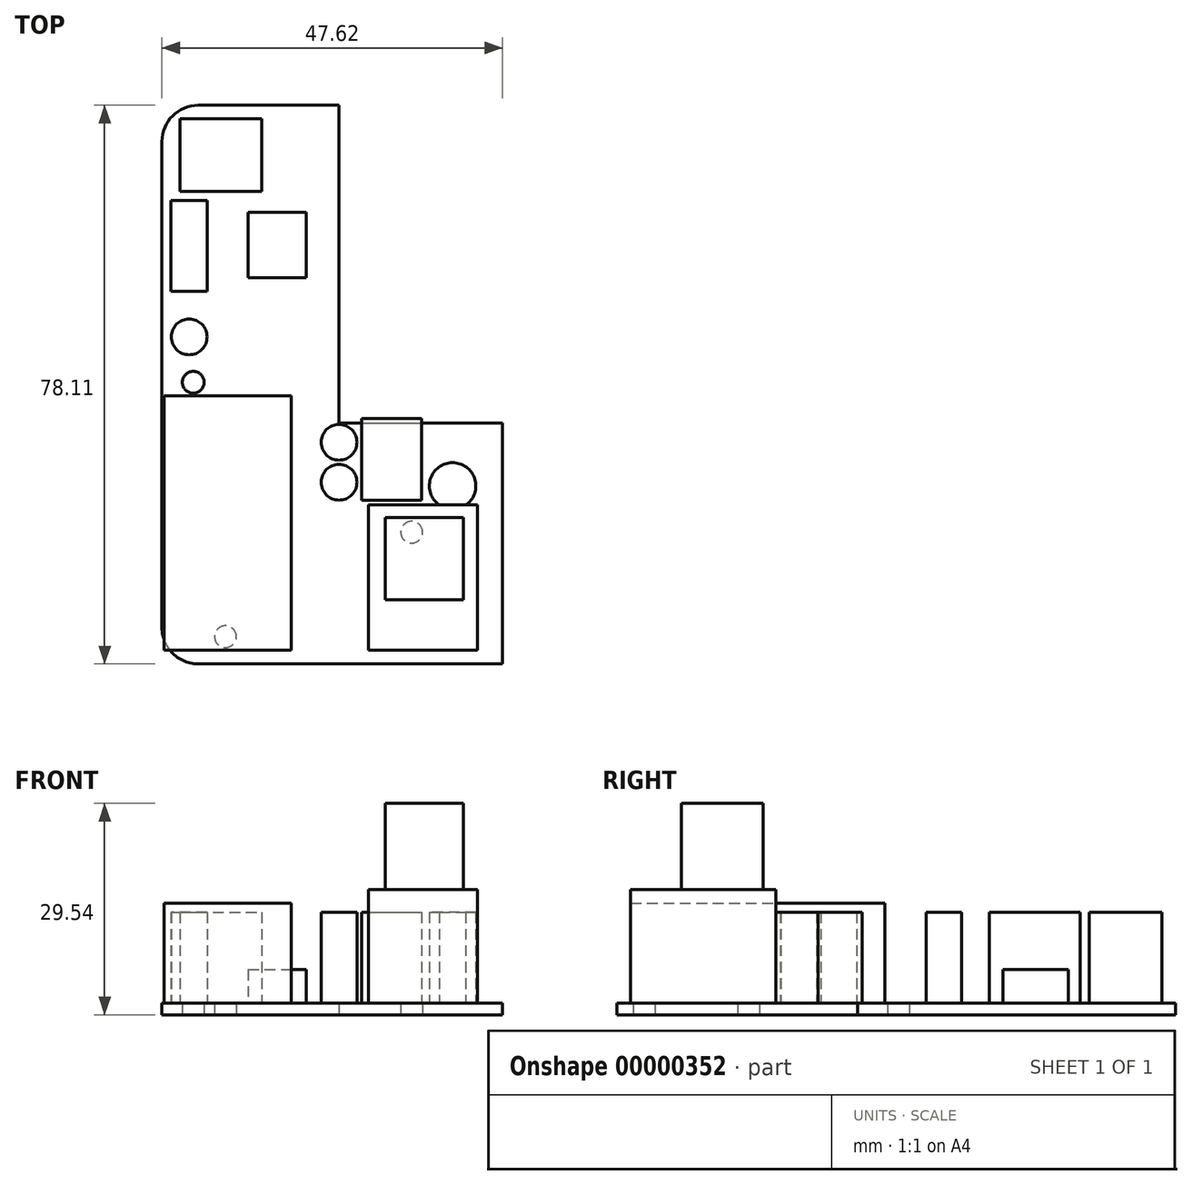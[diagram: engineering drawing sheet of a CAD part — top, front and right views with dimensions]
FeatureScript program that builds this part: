
annotation { "Feature Type Name" : "Feature", "Feature Type Description" : "" }
export const myFeature = defineFeature(function(context is Context, id is Id, definition is map)
    precondition{}
    {
        {
            var Q0;
            Q0=qCreatedBy(makeId("Top.planeOp"),FACE);
            var sketch = newSketch(context, id + "F0", { "sketchPlane" : qUnion([Q0])});
            skLineSegment(sketch, "E0.bottom", {"start": v(5.08, 78.1) * mm, "end": v(24.76, 78.1) * mm});
            skLineSegment(sketch, "E0.top", {"start": v(5.08, 0) * mm, "end": v(24.77, 0) * mm});
            skLineSegment(sketch, "E0.left", {"start": v(0, 73.03) * mm, "end": v(0, 5.08) * mm});
            skLineSegment(sketch, "E0.right", {"start": v(24.76, 78.1) * mm, "end": v(24.77, 33.65) * mm});
            skLineSegment(sketch, "E1.bottom", {"start": v(24.77, 0) * mm, "end": v(47.62, 0) * mm});
            skLineSegment(sketch, "E1.top", {"start": v(24.77, 33.65) * mm, "end": v(47.62, 33.65) * mm});
            skLineSegment(sketch, "E1.right", {"start": v(47.63, 0) * mm, "end": v(47.62, 33.65) * mm});
            skPoint(sketch, "E2.visualSharp", {"position": v(0, 78.1) * mm});
            skArc(sketch, "E2.filletArc", {"start": v(5.08, 78.1) * mm, "mid": v(1.49, 76.62) * mm, "end": v(0, 73.03) * mm});
            skPoint(sketch, "E3.visualSharp", {"position": v(0, 0) * mm});
            skArc(sketch, "E3.filletArc", {"start": v(0, 5.08) * mm, "mid": v(1.49, 1.49) * mm, "end": v(5.08, 0) * mm});
            skCircle(sketch, "E4", {"center": v(4.38, 39.38) * mm, "radius": 1.52 * mm});
            skCircle(sketch, "E5", {"center": v(8.9, 3.81) * mm, "radius": 1.52 * mm});
            skCircle(sketch, "E6", {"center": v(34.92, 18.41) * mm, "radius": 1.52 * mm});
            skSolve(sketch);
        }
        {
            var Q0;
            Q0=qSketchRegion(id+"F0",true);
            extrude(context, id + "F1", {"entities" : qUnion([Q0]), "depth" : 1.6 * mm});
        }
        {
            var Q0;
            Q0=makeQuery(id+"F1.opExtrude","CAP_FACE",FACE,{"disambiguationData":[OSD([sQuery(id+"F0.wireOp",EDGE,"E0.bottom"),sQuery(id+"F0.wireOp",EDGE,"E0.top"),sQuery(id+"F0.wireOp",EDGE,"E0.left"),sQuery(id+"F0.wireOp",EDGE,"E0.right"),sQuery(id+"F0.wireOp",EDGE,"E1.bottom"),sQuery(id+"F0.wireOp",EDGE,"E1.top"),sQuery(id+"F0.wireOp",EDGE,"E1.right"),sQuery(id+"F0.wireOp",EDGE,"E2.filletArc"),sQuery(id+"F0.wireOp",EDGE,"E3.filletArc"),sQuery(id+"F0.wireOp",EDGE,"E4"),sQuery(id+"F0.wireOp",EDGE,"E5"),sQuery(id+"F0.wireOp",EDGE,"E6")])],"isStart":false});
            var sketch = newSketch(context, id + "F2", { "sketchPlane" : qUnion([Q0])});
            skLineSegment(sketch, "E7.bottom", {"start": v(2.54, 76.2) * mm, "end": v(13.97, 76.2) * mm});
            skLineSegment(sketch, "E7.top", {"start": v(2.54, 66.04) * mm, "end": v(13.97, 66.04) * mm});
            skLineSegment(sketch, "E7.left", {"start": v(2.54, 76.2) * mm, "end": v(2.54, 66.04) * mm});
            skLineSegment(sketch, "E7.right", {"start": v(13.97, 76.2) * mm, "end": v(13.97, 66.04) * mm});
            skLineSegment(sketch, "E8.bottom", {"start": v(1.27, 64.77) * mm, "end": v(6.35, 64.77) * mm});
            skLineSegment(sketch, "E8.top", {"start": v(1.27, 52.07) * mm, "end": v(6.35, 52.07) * mm});
            skLineSegment(sketch, "E8.left", {"start": v(1.27, 64.77) * mm, "end": v(1.27, 52.07) * mm});
            skLineSegment(sketch, "E8.right", {"start": v(6.35, 64.77) * mm, "end": v(6.35, 52.07) * mm});
            skLineSegment(sketch, "E9.bottom", {"start": v(27.94, 34.3) * mm, "end": v(36.32, 34.3) * mm});
            skLineSegment(sketch, "E9.top", {"start": v(27.94, 22.86) * mm, "end": v(36.32, 22.86) * mm});
            skLineSegment(sketch, "E9.left", {"start": v(27.94, 34.3) * mm, "end": v(27.94, 22.86) * mm});
            skLineSegment(sketch, "E9.right", {"start": v(36.32, 34.3) * mm, "end": v(36.32, 22.86) * mm});
            skCircle(sketch, "E10", {"center": v(40.64, 24.9) * mm, "radius": 3.25 * mm});
            skCircle(sketch, "E11", {"center": v(24.77, 30.99) * mm, "radius": 2.5 * mm});
            skCircle(sketch, "E12", {"center": v(24.77, 25.4) * mm, "radius": 2.5 * mm});
            skCircle(sketch, "E13", {"center": v(3.81, 45.72) * mm, "radius": 2.5 * mm});
            skLineSegment(sketch, "E14.0", {"start": v(47.62, 0) * mm, "end": v(47.62, 33.65) * mm, "construction": true});
            skSolve(sketch);
        }
        {
            var Q0;
            Q0=qSketchRegion(id+"F2",true);
            extrude(context, id + "F3", {"entities" : qUnion([Q0]), "operationType" : NewBodyOperationType.ADD, "depth" : 12.7 * mm});
        }
        {
            var Q0;
            Q0=makeQuery(id+"F1.opExtrude","CAP_FACE",FACE,{"disambiguationData":[OSD([sQuery(id+"F0.wireOp",EDGE,"E0.bottom"),sQuery(id+"F0.wireOp",EDGE,"E0.top"),sQuery(id+"F0.wireOp",EDGE,"E0.left"),sQuery(id+"F0.wireOp",EDGE,"E0.right"),sQuery(id+"F0.wireOp",EDGE,"E1.bottom"),sQuery(id+"F0.wireOp",EDGE,"E1.top"),sQuery(id+"F0.wireOp",EDGE,"E1.right"),sQuery(id+"F0.wireOp",EDGE,"E2.filletArc"),sQuery(id+"F0.wireOp",EDGE,"E3.filletArc"),sQuery(id+"F0.wireOp",EDGE,"E4"),sQuery(id+"F0.wireOp",EDGE,"E5"),sQuery(id+"F0.wireOp",EDGE,"E6")])],"isStart":false});
            var sketch = newSketch(context, id + "F4", { "sketchPlane" : qUnion([Q0])});
            skLineSegment(sketch, "E15.bottom", {"start": v(12.06, 63.12) * mm, "end": v(20.2, 63.12) * mm});
            skLineSegment(sketch, "E15.top", {"start": v(12.06, 53.98) * mm, "end": v(20.2, 53.98) * mm});
            skLineSegment(sketch, "E15.left", {"start": v(12.06, 63.12) * mm, "end": v(12.06, 53.98) * mm});
            skLineSegment(sketch, "E15.right", {"start": v(20.2, 63.12) * mm, "end": v(20.2, 53.98) * mm});
            skSolve(sketch);
        }
        {
            var Q0;
            Q0=qSketchRegion(id+"F4",true);
            extrude(context, id + "F5", {"entities" : qUnion([Q0]), "operationType" : NewBodyOperationType.ADD, "depth" : 4.7 * mm});
        }
        {
            var Q0;
            Q0=makeQuery(id+"F1.opExtrude","CAP_FACE",FACE,{"disambiguationData":[OSD([sQuery(id+"F0.wireOp",EDGE,"E0.bottom"),sQuery(id+"F0.wireOp",EDGE,"E0.top"),sQuery(id+"F0.wireOp",EDGE,"E0.left"),sQuery(id+"F0.wireOp",EDGE,"E0.right"),sQuery(id+"F0.wireOp",EDGE,"E1.bottom"),sQuery(id+"F0.wireOp",EDGE,"E1.top"),sQuery(id+"F0.wireOp",EDGE,"E1.right"),sQuery(id+"F0.wireOp",EDGE,"E2.filletArc"),sQuery(id+"F0.wireOp",EDGE,"E3.filletArc"),sQuery(id+"F0.wireOp",EDGE,"E4"),sQuery(id+"F0.wireOp",EDGE,"E5"),sQuery(id+"F0.wireOp",EDGE,"E6")])],"isStart":false});
            var sketch = newSketch(context, id + "F6", { "sketchPlane" : qUnion([Q0])});
            skLineSegment(sketch, "E16.bottom", {"start": v(0.32, 1.9) * mm, "end": v(18.1, 1.9) * mm});
            skLineSegment(sketch, "E16.top", {"start": v(0.32, 37.46) * mm, "end": v(18.1, 37.46) * mm});
            skLineSegment(sketch, "E16.left", {"start": v(0.32, 1.9) * mm, "end": v(0.32, 37.46) * mm});
            skLineSegment(sketch, "E16.right", {"start": v(18.1, 1.9) * mm, "end": v(18.1, 37.46) * mm});
            skSolve(sketch);
        }
        {
            var Q0;
            Q0=qSketchRegion(id+"F6",true);
            extrude(context, id + "F7", {"entities" : qUnion([Q0]), "operationType" : NewBodyOperationType.ADD, "depth" : 13.97 * mm});
        }
        {
            var Q0;
            Q0=makeQuery(id+"F1.opExtrude","CAP_FACE",FACE,{"disambiguationData":[OSD([sQuery(id+"F0.wireOp",EDGE,"E0.bottom"),sQuery(id+"F0.wireOp",EDGE,"E0.top"),sQuery(id+"F0.wireOp",EDGE,"E0.left"),sQuery(id+"F0.wireOp",EDGE,"E0.right"),sQuery(id+"F0.wireOp",EDGE,"E1.bottom"),sQuery(id+"F0.wireOp",EDGE,"E1.top"),sQuery(id+"F0.wireOp",EDGE,"E1.right"),sQuery(id+"F0.wireOp",EDGE,"E2.filletArc"),sQuery(id+"F0.wireOp",EDGE,"E3.filletArc"),sQuery(id+"F0.wireOp",EDGE,"E4"),sQuery(id+"F0.wireOp",EDGE,"E5"),sQuery(id+"F0.wireOp",EDGE,"E6")])],"isStart":false});
            var sketch = newSketch(context, id + "F8", { "sketchPlane" : qUnion([Q0])});
            skLineSegment(sketch, "E17.bottom", {"start": v(44.13, 1.9) * mm, "end": v(28.9, 1.9) * mm});
            skLineSegment(sketch, "E17.top", {"start": v(44.13, 22.23) * mm, "end": v(28.9, 22.23) * mm});
            skLineSegment(sketch, "E17.left", {"start": v(44.13, 1.9) * mm, "end": v(44.13, 22.23) * mm});
            skLineSegment(sketch, "E17.right", {"start": v(28.9, 1.9) * mm, "end": v(28.9, 22.23) * mm});
            skSolve(sketch);
        }
        {
            var Q0;
            Q0=qSketchRegion(id+"F8",true);
            extrude(context, id + "F9", {"entities" : qUnion([Q0]), "operationType" : NewBodyOperationType.ADD, "depth" : 15.88 * mm});
        }
        {
            var Q0;
            Q0=makeQuery(id+"F9.opExtrude","CAP_FACE",FACE,{"disambiguationData":[OSD([sQuery(id+"F8.wireOp",EDGE,"E17.bottom"),sQuery(id+"F8.wireOp",EDGE,"E17.top"),sQuery(id+"F8.wireOp",EDGE,"E17.left"),sQuery(id+"F8.wireOp",EDGE,"E17.right")])],"isStart":false});
            var sketch = newSketch(context, id + "F10", { "sketchPlane" : qUnion([Q0])});
            skLineSegment(sketch, "E18.bottom", {"start": v(31.2, 20.46) * mm, "end": v(42.14, 20.46) * mm});
            skLineSegment(sketch, "E18.top", {"start": v(31.2, 9) * mm, "end": v(42.14, 9) * mm});
            skLineSegment(sketch, "E18.left", {"start": v(31.2, 20.46) * mm, "end": v(31.2, 9) * mm});
            skLineSegment(sketch, "E18.right", {"start": v(42.14, 20.46) * mm, "end": v(42.14, 9) * mm});
            skSolve(sketch);
        }
        {
            var Q0;
            Q0=qSketchRegion(id+"F10",true);
            extrude(context, id + "F11", {"entities" : qUnion([Q0]), "operationType" : NewBodyOperationType.ADD, "depth" : 12.06 * mm});
        }
    });
